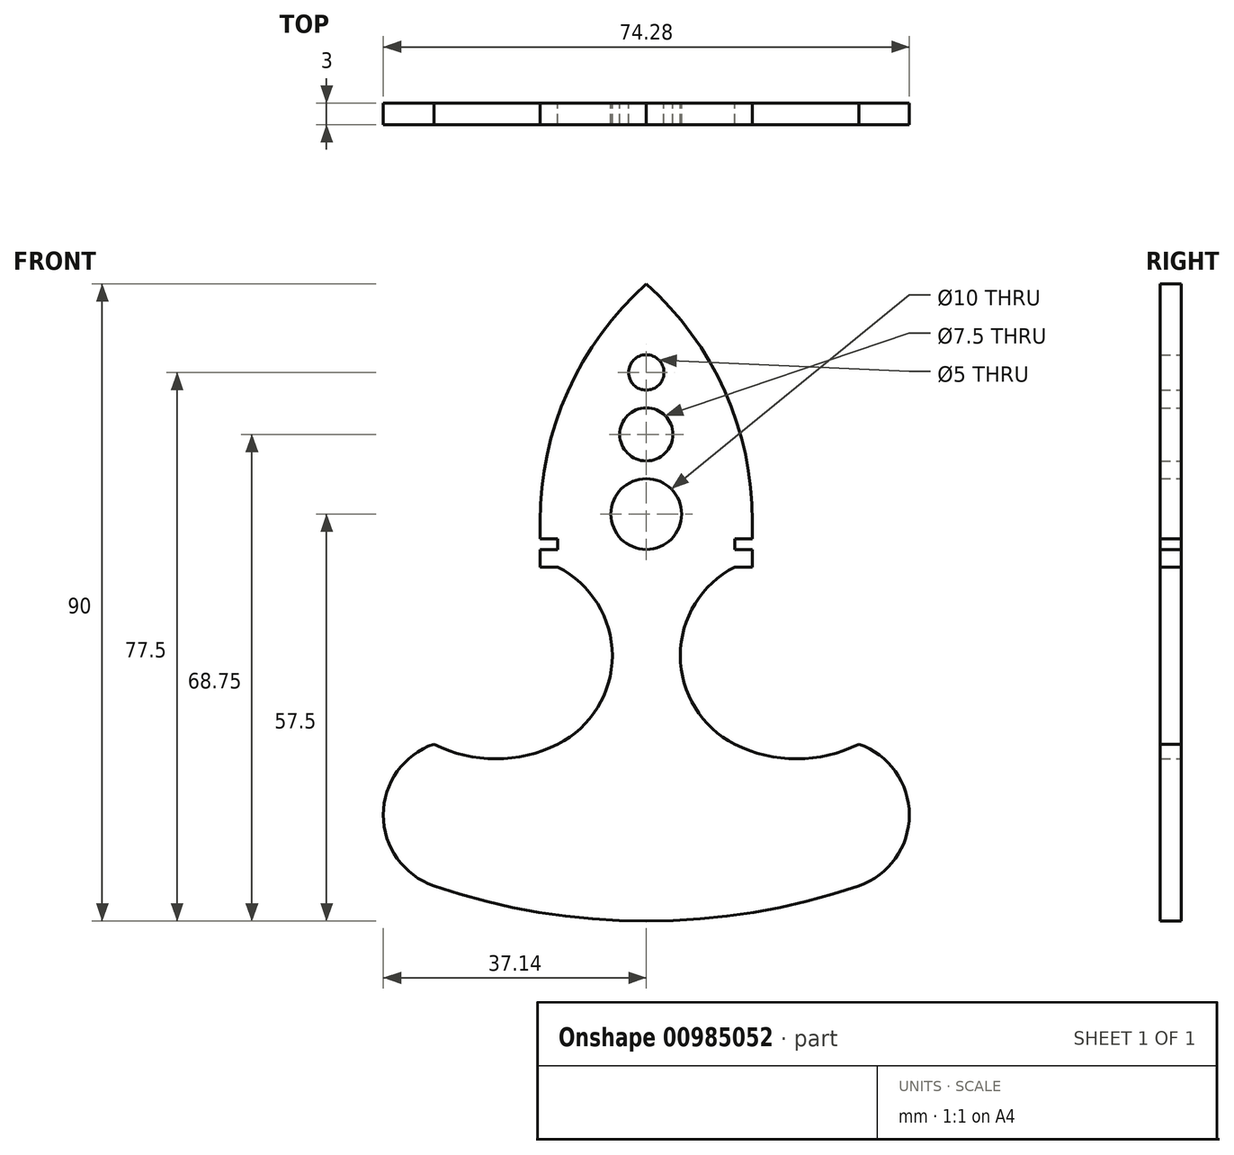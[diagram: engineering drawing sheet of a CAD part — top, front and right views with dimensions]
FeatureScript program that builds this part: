
annotation { "Feature Type Name" : "Feature", "Feature Type Description" : "" }
export const myFeature = defineFeature(function(context is Context, id is Id, definition is map)
    precondition{}
    {
        {
            var Q0;
            Q0=qCreatedBy(makeId("Front.planeOp"),FACE);
            var sketch = newSketch(context, id + "F0", { "sketchPlane" : qUnion([Q0])});
            skPoint(sketch, "E0", {"position": v(0, 40) * mm});
            skPoint(sketch, "E1", {"position": v(-15, 0) * mm});
            skPoint(sketch, "E2", {"position": v(15, 0) * mm});
            skPoint(sketch, "E3", {"position": v(0, -50) * mm});
            skLineSegment(sketch, "E4", {"start": v(-15, 0) * mm, "end": v(-12.5, 0) * mm});
            skLineSegment(sketch, "E5", {"start": v(15, 0) * mm, "end": v(12.5, 0) * mm});
            skPoint(sketch, "E6", {"position": v(-12.5, -25) * mm});
            skPoint(sketch, "E7", {"position": v(12.5, -25) * mm});
            skArc(sketch, "E8", {"start": v(-12.5, -25) * mm, "mid": v(-4.8, -12.5) * mm, "end": v(-12.5, 0) * mm});
            skArc(sketch, "E9", {"start": v(12.5, 0) * mm, "mid": v(4.8, -12.5) * mm, "end": v(12.5, -25) * mm});
            skLineSegment(sketch, "E10", {"start": v(-15, 0) * mm, "end": v(-15, 2.5) * mm});
            skLineSegment(sketch, "E11", {"start": v(15, 0) * mm, "end": v(15, 2.5) * mm});
            skLineSegment(sketch, "E12", {"start": v(-15, 2.5) * mm, "end": v(-12.5, 2.5) * mm});
            skLineSegment(sketch, "E13", {"start": v(15, 2.5) * mm, "end": v(12.5, 2.5) * mm});
            skLineSegment(sketch, "E14", {"start": v(-12.5, 2.5) * mm, "end": v(-12.5, 4) * mm});
            skLineSegment(sketch, "E15", {"start": v(12.5, 2.5) * mm, "end": v(12.5, 4) * mm});
            skLineSegment(sketch, "E16", {"start": v(-12.5, 4) * mm, "end": v(-15, 4) * mm});
            skLineSegment(sketch, "E17", {"start": v(12.5, 4) * mm, "end": v(15, 4) * mm});
            skLineSegment(sketch, "E18", {"start": v(-15, 4) * mm, "end": v(-15, 6.5) * mm});
            skLineSegment(sketch, "E19", {"start": v(15, 4) * mm, "end": v(15, 6.5) * mm});
            skArc(sketch, "E20", {"start": v(-15, 6.5) * mm, "mid": v(-11.08, 24.85) * mm, "end": v(0, 40) * mm});
            skArc(sketch, "E21", {"start": v(15, 6.5) * mm, "mid": v(11.08, 24.85) * mm, "end": v(0, 40) * mm});
            skPoint(sketch, "E22", {"position": v(-30, -45) * mm});
            skPoint(sketch, "E23", {"position": v(30, -45) * mm});
            skArc(sketch, "E24", {"start": v(-30, -45) * mm, "mid": v(0, -50) * mm, "end": v(30, -45) * mm});
            skPoint(sketch, "E25", {"position": v(-30, -25) * mm});
            skPoint(sketch, "E26", {"position": v(30, -25) * mm});
            skArc(sketch, "E27", {"start": v(30, -45) * mm, "mid": v(37.14, -35) * mm, "end": v(30, -25) * mm});
            skArc(sketch, "E28", {"start": v(12.5, -25) * mm, "mid": v(21.25, -27.08) * mm, "end": v(30, -25) * mm});
            skCircle(sketch, "E29", {"center": v(0, 7.5) * mm, "radius": 5 * mm});
            skCircle(sketch, "E30", {"center": v(0, 18.75) * mm, "radius": 3.75 * mm});
            skCircle(sketch, "E31", {"center": v(0, 27.5) * mm, "radius": 2.5 * mm});
            skArc(sketch, "E32", {"start": v(-30, -45) * mm, "mid": v(-37.14, -35) * mm, "end": v(-30, -25) * mm});
            skArc(sketch, "E33", {"start": v(-12.5, -25) * mm, "mid": v(-21.25, -27.08) * mm, "end": v(-30, -25) * mm});
            skSolve(sketch);
        }
        {
            var Q0;
            Q0=makeQuery(id+"F0.imprint","IMPRINT",FACE,{"disambiguationData":[TD([[makeQuery(id+"F0.imprint","IMPRINT",EDGE,{"derivedFrom":sQuery(id+"F0.wireOp",EDGE,"E4")}),1.0]])]});
            extrude(context, id + "F1", {"entities" : qUnion([Q0]), "endBound" : BoundingType.SYMMETRIC, "depth" : 3 * mm, "offsetDistance" : 25 * mm});
        }
    });
